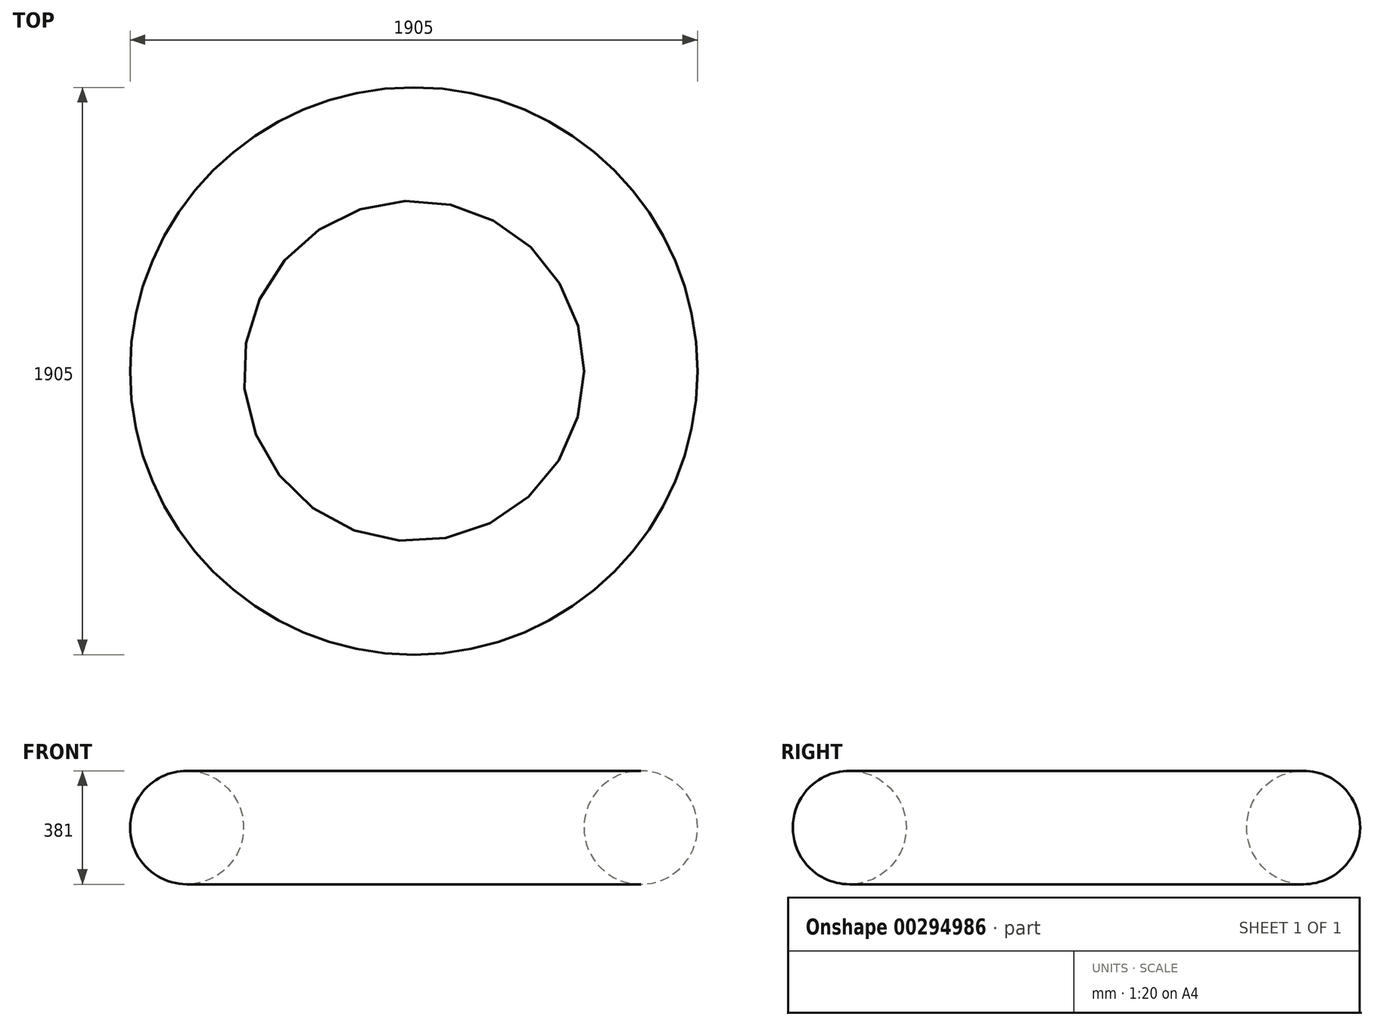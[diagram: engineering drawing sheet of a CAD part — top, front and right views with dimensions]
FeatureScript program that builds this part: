
annotation { "Feature Type Name" : "Feature", "Feature Type Description" : "" }
export const myFeature = defineFeature(function(context is Context, id is Id, definition is map)
    precondition{}
    {
        {
            var Q0;
            Q0=qCreatedBy(makeId("Front.planeOp"),FACE);
            var sketch = newSketch(context, id + "F0", { "sketchPlane" : qUnion([Q0])});
            skCircle(sketch, "E0", {"center": v(762, 0) * mm, "radius": 190.5 * mm});
            skSolve(sketch);
        }
        {
            var Q0;
            Q0=qCreatedBy(makeId("Front.planeOp"),FACE);
            var sketch = newSketch(context, id + "F1", { "sketchPlane" : qUnion([Q0])});
            skLineSegment(sketch, "E1", {"start": v(0, 136.68) * mm, "end": v(0, -200.24) * mm, "construction": true});
            skSolve(sketch);
        }
        {
            var Q0;
            Q0=makeQuery(id+"F0.imprint","IMPRINT",FACE,{"disambiguationData":[TD([[makeQuery(id+"F0.imprint","IMPRINT",EDGE,{"derivedFrom":sQuery(id+"F0.wireOp",EDGE,"E0")}),1.0]])]});
            var Q1;
            Q1=sQuery(id+"F1.wireOp",EDGE,"E1");
            revolve(context, id + "F2", {"entities" : qUnion([Q0]), "axis" : qUnion([Q1]), "revolveType" : RevolveType.FULL});
        }
    });
